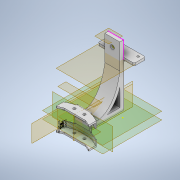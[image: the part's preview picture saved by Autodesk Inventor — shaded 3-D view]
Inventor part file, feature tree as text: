
AUTODESK INVENTOR PART (.ipt)
format: ipt  version: 2021 (Build 250183000, 183)  size: 5,300,736 bytes
history: native  units: mm
features: sketch x33, move_body x21, extrude x20, other x20, direct_edit x20, plane x14, projected_geometry x11, delete_face x8, mirror x6, fillet x6, sweep x2, revolve x2, thread x1
ambient origin geometry x8: Origin, YZ Plane, XZ Plane, XY Plane, X Axis, Y Axis, Z Axis, Center Point
bodies: Solid1 (feature_tree), Solid2 (feature_tree), Solid3 (feature_tree), Solid4 (feature_tree), Solid5 (feature_tree), Solid6 (feature_tree)
feature tree (164):
  sketch  "Sketch7"  dims[d10=10.0mm d11=31.4mm]
  plane  "Work Plane4"
  sketch  "Sketch8"  dims[d13=100.0mm d33=100.0mm]
  plane  "Work Plane5"
  plane  "Work Plane7"
  mirror  "Mirror4"
  sweep  "Sweep5"
  sketch  "Sketch15"  dims[d38=7.0mm d39=1.0mm]
  plane  "Work Plane13"
  extrude  "Extrusion7"  Depth=100.0mm
  mirror  "Mirror6"
  mirror  "Mirror7"
  extrude  "Extrusion8"  Depth=100.0mm
  plane  "Work Plane14"
  mirror  "Mirror8"
  mirror  "Mirror9"
  extrude  "Extrusion9"  Depth=1.0mm
  sketch  "Sketch18"  dims[d45=3.5mm d46=1.0mm]
  plane  "Work Plane15"
  plane  "Work Plane16"
  plane  "Work Plane17"
  extrude  "Extrusion11"  Depth=1.0mm
  fillet  "Fillet5"  Radius=9.0mm
  plane  "Work Plane20"
  mirror  "Mirror10"
  extrude  "Extrusion12"  Depth=1.0mm
  sweep  "Sweep6"
  extrude  "Extrusion13"  Depth=5.0mm
  fillet  "Fillet7"  Radius=1.0mm
  extrude  "Extrusion14"  TaperAngle=0.0deg  [1 undecoded]
  extrude  "Extrusion15"  Depth=1.0mm TaperAngle=0.0deg
  fillet  "Fillet8"  Radius=3.0mm
  extrude  "Extrusion16"  Depth=38.5mm TaperAngle=0.0deg
  extrude  "Extrusion17"  Depth=2.0mm
  extrude  "Extrusion18"  Depth=166.75mm TaperAngle=0.0deg
  extrude  "Extrusion19"  Depth=2.0mm TaperAngle=0.0deg
  extrude  "Extrusion20"  Depth=13.25mm TaperAngle=0.0deg
  extrude  "Extrusion21"  Depth=2.0mm
  sketch  "Sketch32"  dims[d125=-36.254mm d126=16.5mm d127=86.882mm d128=-1.25mm d129=0.0mm d130=0.0mm]
  plane  "Work Plane22"
  sketch  "Sketch33"  dims[d131=0.0mm d132=0.0mm d133=0.1mm d136=0.0mm d137=0.0mm d138=51.5mm]
  plane  "Work Plane23"
  extrude  "Extrusion22"  Depth=13.25mm TaperAngle=0.0deg
  fillet  "Fillet9"  Radius=5.5mm
  sketch  "Sketch34"  dims[d139=10.0mm d140=0.0mm d141=10.0mm d142=0.0mm]
  other  "Split2[2]"
  thread  "Thread1"  [1 undecoded]
  other  "Cut-Extrude10[1]"
  other  "Cut-Extrude10[2]"
  other  "Cut-Extrude12"
  direct_edit  "Direct Edit1"
  direct_edit  "Direct Edit2"
  direct_edit  "Direct Edit3"
  sketch  "Sketch35"  dims[d145=2.0mm d146=-4.75mm]
  direct_edit  "Direct Edit4"
  sketch  "Sketch37"  dims[d148=1.5mm]
  direct_edit  "Direct Edit5"
  extrude  "Extrusion24"  Depth=10.0mm
  plane  "Work Plane24"
  extrude  "Extrusion25"  Depth=10.0mm TaperAngle=0.0deg
  delete_face  "Delete Face1"
  delete_face  "Delete Face2"
  delete_face  "Delete Face3"
  delete_face  "Delete Face4"
  delete_face  "Delete Face5"
  delete_face  "Delete Face6"
  delete_face  "Delete Face7"
  delete_face  "Delete Face8"
  fillet  "Fillet10"  Radius=2.0mm
  direct_edit  "Direct Edit7"
  direct_edit  "Direct Edit8"
  extrude  "Extrusion27"  Depth=31.4mm
  fillet  "Fillet11"  Radius=31.4mm
  direct_edit  "Direct Edit9"
  direct_edit  "Direct Edit10"
  direct_edit  "Direct Edit11"
  direct_edit  "Direct Edit12"
  direct_edit  "Direct Edit13"
  direct_edit  "Direct Edit14"
  direct_edit  "Direct Edit15"
  direct_edit  "Direct Edit16"
  direct_edit  "Direct Edit17"
  direct_edit  "Direct Edit18"
  sketch  "Sketch42"  dims[d152=1.5mm]
  direct_edit  "Direct Edit19"
  extrude  "Extrusion28"  TaperAngle=0.0deg  [1 undecoded]
  sketch  "Sketch36"  dims[d147=-7.25mm]
  extrude  "Extrusion29"  Depth=51.5mm TaperAngle=0.0deg
  direct_edit  "Direct Edit20"
  direct_edit  "Direct Edit21"
  sketch  "Sketch44"  dims[d155=2.0mm]
  sketch  "Sketch45"  dims[d156=1.25mm d157=1.25mm d158=0.0mm d159=0.0mm d160=-1.25mm d161=0.0mm d162=0.0mm d163=-0.25mm d164=0.0mm d165=0.0mm d166=1.0mm d167=-0.5mm d168=0.0mm d169=0.0mm d170=1.75mm d171=0.0mm d172=0.0mm d173=4.0mm d174=0.0mm d175=-2.5mm d176=0.0mm d177=0.0mm d178=0.0mm d179=-46.5mm d180=0.0mm d181=0.0mm d182=-46.5mm d183=0.0mm d184=0.0mm d185=-1.0mm d186=0.0mm d187=0.0mm d188=-0.5mm d189=0.0mm d190=0.0mm d191=1.5mm d192=0.0mm d193=0.0mm d194=-6.5mm d195=0.0mm d196=0.0mm d197=-4.5mm d198=0.0mm d199=0.0mm d200=-0.5mm d201=0.0mm d202=0.0mm d203=-0.5mm d204=0.0mm d205=0.0mm d206=0.5mm d207=0.0mm d208=0.0mm d209=0.5mm d210=6.0mm d211=90.0mm d212=10.0mm d213=0.0mm d214=10.0mm d215=0.0mm d216=-4.0mm d217=-0.5mm]
  plane  "Work Plane9"
  sketch  "Sketch13"  dims[d36=100.0mm d37=100.0mm]
  projected_geometry  "Projected Loop5"
  sketch  "Sketch16"  dims[d40=9.0mm d41=1.0mm d42=9.0mm]
  sketch  "Sketch17"  dims[d43=3.5mm d44=1.0mm]
  sketch  "Sketch19"  dims[d47=1.0mm d48=5.0mm d49=1.0mm]
  sketch  "Sketch20"  dims[d50=5.0mm d71=0.0mm d72=0.0mm]
  sketch  "Sketch21"  dims[d75=1.0mm d76=0.0mm d77=1.0mm d78=0.0mm d79=3.0mm]
  sketch  "Sketch22"  dims[d80=3.0mm d81=38.5mm d82=0.0mm]
  sketch  "Sketch23"  dims[d85=2.0mm d86=2.0mm d87=0.0mm d88=0.0mm d89=2.0mm]
  projected_geometry  "Projected Loop10"
  projected_geometry  "Projected Loop11"
  sketch  "Sketch24"  dims[d92=25.0mm d93=166.75mm d94=0.0mm]
  projected_geometry  "Projected Loop12"
  sketch  "Sketch25"  dims[d95=0.0mm d96=0.0mm d98=2.0mm d99=0.0mm]
  sketch  "Sketch26"  dims[d100=2.0mm d101=13.25mm d102=0.0mm]
  sketch  "Sketch27"  dims[d103=13.25mm d104=0.0mm d105=2.0mm]
  projected_geometry  "Projected Loop13"
  sketch  "Sketch28"  dims[d106=13.25mm d107=0.0mm d108=13.25mm d109=0.0mm d110=5.5mm d111=0.0mm d112=0.0mm d113=0.0mm]
  projected_geometry  "Projected Loop14"
  projected_geometry  "Projected Loop15"
  sketch  "Sketch29"  dims[d114=10.0mm d115=0.0mm d116=5.5mm]
  sketch  "Sketch30"  dims[d117=10.0mm d118=0.0mm d119=10.0mm d120=0.0mm d121=2.0mm]
  sketch  "Sketch31"  dims[d122=6.9mm d123=31.4mm d124=31.4mm]
  plane  "Work Plane21"
  projected_geometry  "Projected Loop16"
  projected_geometry  "Projected Loop17"
  sketch  "Sketch38"  dims[d149=1.5mm]
  projected_geometry  "Projected Loop18"
  sketch  "Sketch39"  dims[d150=1.5mm]
  projected_geometry  "Projected Loop19"
  sketch  "Sketch41"  dims[d151=1.5mm]
  sketch  "Sketch43"  dims[d153=10.0mm d154=0.0mm]
  other  "Cavity6"
  revolve  "Rotate1"  [1 undecoded]
  revolve  "Rotate2"  [1 undecoded]
  move_body  "Move1"
  move_body  "Move2"
  move_body  "Move3"
  move_body  "Move4"
  other  "Size1"
  other  "Size2"
  other  "Size3"
  other  "Size4"
  other  "Size5"
  other  "Size6"
  other  "Size7"
  other  "Size8"
  other  "Size9"
  move_body  "Move5"
  move_body  "Move6"
  move_body  "Move7"
  other  "Size10"
  move_body  "Move8"
  move_body  "Move9"
  move_body  "Move10"
  move_body  "Move11"
  move_body  "Move12"
  move_body  "Move13"
  move_body  "Move14"
  move_body  "Move15"
  move_body  "Move16"
  move_body  "Move17"
  move_body  "Move18"
  move_body  "Move19"
  move_body  "Move20"
  move_body  "Move21"
  other  "Size11"
  other  "Size12"
  parser-record x1  (decoder bookkeeping rows leaked as tree rows — omitted from the tree; the rows remain in map.json)
  other  "whole_assembly.iam"
  other  "Intel Realsense D435:1"
note: 5 required parameter values undecoded (feature->parameter linkage not recoverable at this tier; creation-order binding heuristic only, values carry confidence <= 0.55)
note: 1 file-system path scrubbed to <path> (originals preserved in map.json)